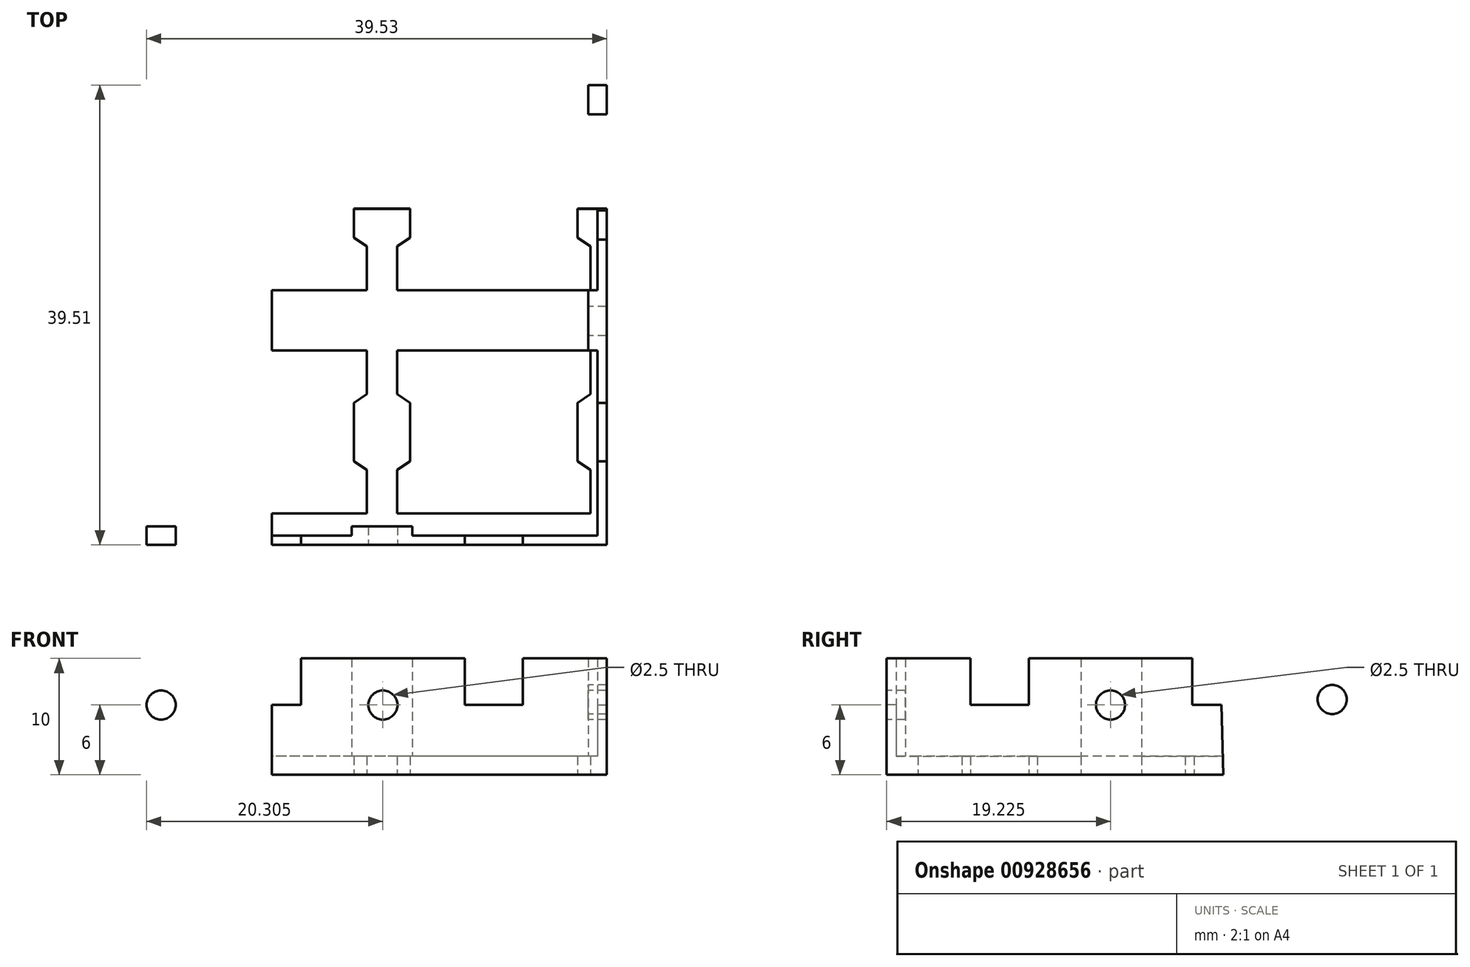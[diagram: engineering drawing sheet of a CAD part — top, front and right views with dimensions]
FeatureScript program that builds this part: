
annotation { "Feature Type Name" : "Feature", "Feature Type Description" : "" }
export const myFeature = defineFeature(function(context is Context, id is Id, definition is map)
    precondition{}
    {
        {
            var Q0;
            Q0=qCreatedBy(makeId("Top.planeOp"),FACE);
            var sketch = newSketch(context, id + "F0", { "sketchPlane" : qUnion([Q0])});
            skLineSegment(sketch, "E0.bottom", {"start": v(-1.4, 2.7) * mm, "end": v(-18, 2.7) * mm});
            skLineSegment(sketch, "E0.top", {"start": v(-1.4, 16.7) * mm, "end": v(-18, 16.7) * mm});
            skLineSegment(sketch, "E0.left", {"start": v(-1.4, 2.7) * mm, "end": v(-1.4, 16.7) * mm});
            skLineSegment(sketch, "E0.right", {"start": v(-18, 2.7) * mm, "end": v(-18, 16.7) * mm});
            skLineSegment(sketch, "E1", {"start": v(-1.4, 12.95) * mm, "end": v(-2.5, 12.2) * mm});
            skLineSegment(sketch, "E2", {"start": v(-2.5, 12.2) * mm, "end": v(-2.5, 7.2) * mm});
            skLineSegment(sketch, "E3", {"start": v(-2.5, 7.2) * mm, "end": v(-1.4, 6.45) * mm});
            skLineSegment(sketch, "E4", {"start": v(-1.4, 6.45) * mm, "end": v(-1.4, 12.95) * mm});
            skLineSegment(sketch, "E5", {"start": v(-1.4, 12.95) * mm, "end": v(-1.4, 16.7) * mm});
            skLineSegment(sketch, "E6", {"start": v(-1.4, 6.45) * mm, "end": v(-1.4, 2.7) * mm});
            skLineSegment(sketch, "E7", {"start": v(-9.7, 16.7) * mm, "end": v(-9.7, 2.7) * mm});
            skLineSegment(sketch, "E8.MirrorCS", {"start": v(-16.9, 12.2) * mm, "end": v(-16.9, 7.2) * mm});
            skLineSegment(sketch, "E9.MirrorCS", {"start": v(-18, 12.95) * mm, "end": v(-16.9, 12.2) * mm});
            skLineSegment(sketch, "E10.MirrorCS", {"start": v(-16.9, 7.2) * mm, "end": v(-18, 6.45) * mm});
            skLineSegment(sketch, "E11.1.0.0", {"start": v(-20.6, 16.7) * mm, "end": v(-37.2, 16.7) * mm});
            skLineSegment(sketch, "E11.1.0.1", {"start": v(-37.2, 2.7) * mm, "end": v(-37.2, 16.7) * mm});
            skLineSegment(sketch, "E11.1.0.2", {"start": v(-20.6, 2.7) * mm, "end": v(-37.2, 2.7) * mm});
            skLineSegment(sketch, "E11.1.0.3", {"start": v(-20.6, 6.45) * mm, "end": v(-20.6, 2.7) * mm});
            skLineSegment(sketch, "E11.1.0.4", {"start": v(-21.7, 12.2) * mm, "end": v(-21.7, 7.2) * mm});
            skLineSegment(sketch, "E11.1.0.5", {"start": v(-21.7, 7.2) * mm, "end": v(-20.6, 6.45) * mm});
            skLineSegment(sketch, "E11.1.0.6", {"start": v(-20.6, 12.95) * mm, "end": v(-21.7, 12.2) * mm});
            skLineSegment(sketch, "E11.1.0.7", {"start": v(-20.6, 12.95) * mm, "end": v(-20.6, 16.7) * mm});
            skLineSegment(sketch, "E11.1.0.8", {"start": v(-20.6, 6.45) * mm, "end": v(-20.6, 12.95) * mm});
            skLineSegment(sketch, "E11.1.0.9", {"start": v(-36.1, 12.2) * mm, "end": v(-36.1, 7.2) * mm});
            skLineSegment(sketch, "E11.1.0.10", {"start": v(-37.2, 12.95) * mm, "end": v(-36.1, 12.2) * mm});
            skLineSegment(sketch, "E11.1.0.11", {"start": v(-36.1, 7.2) * mm, "end": v(-37.2, 6.45) * mm});
            skLineSegment(sketch, "E11.2.0.0", {"start": v(-39.8, 16.7) * mm, "end": v(-56.4, 16.7) * mm});
            skLineSegment(sketch, "E11.2.0.1", {"start": v(-56.4, 2.7) * mm, "end": v(-56.4, 16.7) * mm});
            skLineSegment(sketch, "E11.2.0.2", {"start": v(-39.8, 2.7) * mm, "end": v(-56.4, 2.7) * mm});
            skLineSegment(sketch, "E11.2.0.3", {"start": v(-39.8, 6.45) * mm, "end": v(-39.8, 2.7) * mm});
            skLineSegment(sketch, "E11.2.0.4", {"start": v(-40.9, 12.2) * mm, "end": v(-40.9, 7.2) * mm});
            skLineSegment(sketch, "E11.2.0.5", {"start": v(-40.9, 7.2) * mm, "end": v(-39.8, 6.45) * mm});
            skLineSegment(sketch, "E11.2.0.6", {"start": v(-39.8, 12.95) * mm, "end": v(-40.9, 12.2) * mm});
            skLineSegment(sketch, "E11.2.0.7", {"start": v(-39.8, 12.95) * mm, "end": v(-39.8, 16.7) * mm});
            skLineSegment(sketch, "E11.2.0.8", {"start": v(-39.8, 6.45) * mm, "end": v(-39.8, 12.95) * mm});
            skLineSegment(sketch, "E11.2.0.9", {"start": v(-55.3, 12.2) * mm, "end": v(-55.3, 7.2) * mm});
            skLineSegment(sketch, "E11.2.0.10", {"start": v(-56.4, 12.95) * mm, "end": v(-55.3, 12.2) * mm});
            skLineSegment(sketch, "E11.2.0.11", {"start": v(-55.3, 7.2) * mm, "end": v(-56.4, 6.45) * mm});
            skLineSegment(sketch, "E11.direction1", {"start": v(-18, 16.7) * mm, "end": v(-37.2, 16.7) * mm, "construction": true});
            skLineSegment(sketch, "E12.bottom", {"start": v(0, 0) * mm, "end": v(-57.8, 0) * mm});
            skLineSegment(sketch, "E12.top", {"start": v(0, 57.8) * mm, "end": v(-57.8, 57.8) * mm});
            skLineSegment(sketch, "E12.left", {"start": v(0, 0) * mm, "end": v(0, 57.8) * mm});
            skLineSegment(sketch, "E12.right", {"start": v(-57.8, 0) * mm, "end": v(-57.8, 57.8) * mm});
            skLineSegment(sketch, "E13", {"start": v(-1.4, 2.7) * mm, "end": v(0, 2.7) * mm});
            skLineSegment(sketch, "E14", {"start": v(-56.4, 2.7) * mm, "end": v(-57.8, 2.7) * mm});
            skLineSegment(sketch, "E15", {"start": v(-1.4, 2.7) * mm, "end": v(-1.4, 0) * mm});
            skLineSegment(sketch, "E16.0.1.0", {"start": v(-39.8, 32.15) * mm, "end": v(-39.8, 35.9) * mm});
            skLineSegment(sketch, "E16.0.1.1", {"start": v(-20.6, 25.65) * mm, "end": v(-20.6, 21.9) * mm});
            skLineSegment(sketch, "E16.0.1.3", {"start": v(-40.9, 31.4) * mm, "end": v(-40.9, 26.4) * mm});
            skLineSegment(sketch, "E16.0.1.4", {"start": v(-1.4, 35.9) * mm, "end": v(-18, 35.9) * mm});
            skLineSegment(sketch, "E16.0.1.5", {"start": v(-1.4, 32.15) * mm, "end": v(-1.4, 35.9) * mm});
            skLineSegment(sketch, "E16.0.1.6", {"start": v(-1.4, 21.9) * mm, "end": v(-18, 21.9) * mm});
            skLineSegment(sketch, "E16.0.1.7", {"start": v(-39.8, 21.9) * mm, "end": v(-56.4, 21.9) * mm});
            skLineSegment(sketch, "E16.0.1.8", {"start": v(-36.1, 31.4) * mm, "end": v(-36.1, 26.4) * mm});
            skLineSegment(sketch, "E16.0.1.9", {"start": v(-39.8, 25.65) * mm, "end": v(-39.8, 21.9) * mm});
            skLineSegment(sketch, "E16.0.1.10", {"start": v(-21.7, 31.4) * mm, "end": v(-21.7, 26.4) * mm});
            skLineSegment(sketch, "E16.0.1.11", {"start": v(-20.6, 32.15) * mm, "end": v(-20.6, 35.9) * mm});
            skLineSegment(sketch, "E16.0.1.12", {"start": v(-20.6, 21.9) * mm, "end": v(-37.2, 21.9) * mm});
            skLineSegment(sketch, "E16.0.1.13", {"start": v(-55.3, 31.4) * mm, "end": v(-55.3, 26.4) * mm});
            skLineSegment(sketch, "E16.0.1.14", {"start": v(-20.6, 25.65) * mm, "end": v(-20.6, 32.15) * mm});
            skLineSegment(sketch, "E16.0.1.15", {"start": v(-2.5, 31.4) * mm, "end": v(-2.5, 26.4) * mm});
            skLineSegment(sketch, "E16.0.1.16", {"start": v(-16.9, 31.4) * mm, "end": v(-16.9, 26.4) * mm});
            skLineSegment(sketch, "E16.0.1.18", {"start": v(-1.4, 25.65) * mm, "end": v(-1.4, 21.9) * mm});
            skLineSegment(sketch, "E16.0.1.19", {"start": v(-39.8, 35.9) * mm, "end": v(-56.4, 35.9) * mm});
            skLineSegment(sketch, "E16.0.1.20", {"start": v(-1.4, 25.65) * mm, "end": v(-1.4, 32.15) * mm});
            skLineSegment(sketch, "E16.0.1.21", {"start": v(-18, 32.15) * mm, "end": v(-16.9, 31.4) * mm});
            skLineSegment(sketch, "E16.0.1.22", {"start": v(-37.2, 32.15) * mm, "end": v(-36.1, 31.4) * mm});
            skLineSegment(sketch, "E16.0.1.23", {"start": v(-1.4, 32.15) * mm, "end": v(-2.5, 31.4) * mm});
            skLineSegment(sketch, "E16.0.1.24", {"start": v(-20.6, 35.9) * mm, "end": v(-37.2, 35.9) * mm});
            skLineSegment(sketch, "E16.0.1.25", {"start": v(-16.9, 26.4) * mm, "end": v(-18, 25.65) * mm});
            skLineSegment(sketch, "E16.0.1.27", {"start": v(-2.5, 26.4) * mm, "end": v(-1.4, 25.65) * mm});
            skLineSegment(sketch, "E16.0.1.28", {"start": v(-36.1, 26.4) * mm, "end": v(-37.2, 25.65) * mm});
            skLineSegment(sketch, "E16.0.1.29", {"start": v(-40.9, 26.4) * mm, "end": v(-39.8, 25.65) * mm});
            skLineSegment(sketch, "E16.0.1.30", {"start": v(-20.6, 32.15) * mm, "end": v(-21.7, 31.4) * mm});
            skLineSegment(sketch, "E16.0.1.31", {"start": v(-56.4, 32.15) * mm, "end": v(-55.3, 31.4) * mm});
            skLineSegment(sketch, "E16.0.1.32", {"start": v(-21.7, 26.4) * mm, "end": v(-20.6, 25.65) * mm});
            skLineSegment(sketch, "E16.0.1.33", {"start": v(-39.8, 32.15) * mm, "end": v(-40.9, 31.4) * mm});
            skLineSegment(sketch, "E16.0.1.34", {"start": v(-55.3, 26.4) * mm, "end": v(-56.4, 25.65) * mm});
            skLineSegment(sketch, "E16.0.1.36", {"start": v(-39.8, 25.65) * mm, "end": v(-39.8, 32.15) * mm});
            skLineSegment(sketch, "E16.0.2.0", {"start": v(-39.8, 51.35) * mm, "end": v(-39.8, 55.1) * mm});
            skLineSegment(sketch, "E16.0.2.1", {"start": v(-20.6, 44.85) * mm, "end": v(-20.6, 41.1) * mm});
            skLineSegment(sketch, "E16.0.2.2", {"start": v(-18, 41.1) * mm, "end": v(-18, 55.1) * mm});
            skLineSegment(sketch, "E16.0.2.3", {"start": v(-40.9, 50.6) * mm, "end": v(-40.9, 45.6) * mm});
            skLineSegment(sketch, "E16.0.2.4", {"start": v(-1.4, 55.1) * mm, "end": v(-18, 55.1) * mm});
            skLineSegment(sketch, "E16.0.2.5", {"start": v(-1.4, 51.35) * mm, "end": v(-1.4, 55.1) * mm});
            skLineSegment(sketch, "E16.0.2.6", {"start": v(-1.4, 41.1) * mm, "end": v(-18, 41.1) * mm});
            skLineSegment(sketch, "E16.0.2.7", {"start": v(-39.8, 41.1) * mm, "end": v(-56.4, 41.1) * mm});
            skLineSegment(sketch, "E16.0.2.8", {"start": v(-36.1, 50.6) * mm, "end": v(-36.1, 45.6) * mm});
            skLineSegment(sketch, "E16.0.2.9", {"start": v(-39.8, 44.85) * mm, "end": v(-39.8, 41.1) * mm});
            skLineSegment(sketch, "E16.0.2.10", {"start": v(-21.7, 50.6) * mm, "end": v(-21.7, 45.6) * mm});
            skLineSegment(sketch, "E16.0.2.11", {"start": v(-20.6, 51.35) * mm, "end": v(-20.6, 55.1) * mm});
            skLineSegment(sketch, "E16.0.2.12", {"start": v(-20.6, 41.1) * mm, "end": v(-37.2, 41.1) * mm});
            skLineSegment(sketch, "E16.0.2.13", {"start": v(-55.3, 50.6) * mm, "end": v(-55.3, 45.6) * mm});
            skLineSegment(sketch, "E16.0.2.14", {"start": v(-20.6, 44.85) * mm, "end": v(-20.6, 51.35) * mm});
            skLineSegment(sketch, "E16.0.2.15", {"start": v(-2.5, 50.6) * mm, "end": v(-2.5, 45.6) * mm});
            skLineSegment(sketch, "E16.0.2.16", {"start": v(-16.9, 50.6) * mm, "end": v(-16.9, 45.6) * mm});
            skLineSegment(sketch, "E16.0.2.17", {"start": v(-37.2, 41.1) * mm, "end": v(-37.2, 55.1) * mm});
            skLineSegment(sketch, "E16.0.2.18", {"start": v(-1.4, 44.85) * mm, "end": v(-1.4, 41.1) * mm});
            skLineSegment(sketch, "E16.0.2.19", {"start": v(-39.8, 55.1) * mm, "end": v(-56.4, 55.1) * mm});
            skLineSegment(sketch, "E16.0.2.20", {"start": v(-1.4, 44.85) * mm, "end": v(-1.4, 51.35) * mm});
            skLineSegment(sketch, "E16.0.2.21", {"start": v(-18, 51.35) * mm, "end": v(-16.9, 50.6) * mm});
            skLineSegment(sketch, "E16.0.2.22", {"start": v(-37.2, 51.35) * mm, "end": v(-36.1, 50.6) * mm});
            skLineSegment(sketch, "E16.0.2.23", {"start": v(-1.4, 51.35) * mm, "end": v(-2.5, 50.6) * mm});
            skLineSegment(sketch, "E16.0.2.24", {"start": v(-20.6, 55.1) * mm, "end": v(-37.2, 55.1) * mm});
            skLineSegment(sketch, "E16.0.2.25", {"start": v(-16.9, 45.6) * mm, "end": v(-18, 44.85) * mm});
            skLineSegment(sketch, "E16.0.2.26", {"start": v(-1.4, 41.1) * mm, "end": v(-1.4, 55.1) * mm});
            skLineSegment(sketch, "E16.0.2.27", {"start": v(-2.5, 45.6) * mm, "end": v(-1.4, 44.85) * mm});
            skLineSegment(sketch, "E16.0.2.28", {"start": v(-36.1, 45.6) * mm, "end": v(-37.2, 44.85) * mm});
            skLineSegment(sketch, "E16.0.2.29", {"start": v(-40.9, 45.6) * mm, "end": v(-39.8, 44.85) * mm});
            skLineSegment(sketch, "E16.0.2.30", {"start": v(-20.6, 51.35) * mm, "end": v(-21.7, 50.6) * mm});
            skLineSegment(sketch, "E16.0.2.31", {"start": v(-56.4, 51.35) * mm, "end": v(-55.3, 50.6) * mm});
            skLineSegment(sketch, "E16.0.2.32", {"start": v(-21.7, 45.6) * mm, "end": v(-20.6, 44.85) * mm});
            skLineSegment(sketch, "E16.0.2.33", {"start": v(-39.8, 51.35) * mm, "end": v(-40.9, 50.6) * mm});
            skLineSegment(sketch, "E16.0.2.34", {"start": v(-55.3, 45.6) * mm, "end": v(-56.4, 44.85) * mm});
            skLineSegment(sketch, "E16.0.2.35", {"start": v(-56.4, 41.1) * mm, "end": v(-56.4, 55.1) * mm});
            skLineSegment(sketch, "E16.0.2.36", {"start": v(-39.8, 44.85) * mm, "end": v(-39.8, 51.35) * mm});
            skLineSegment(sketch, "E16.direction1", {"start": v(-56.4, 2.7) * mm, "end": v(-34.05, 2.7) * mm, "construction": true});
            skLineSegment(sketch, "E16.direction2", {"start": v(-56.4, 2.7) * mm, "end": v(-56.4, 21.9) * mm, "construction": true});
            skLineSegment(sketch, "E17", {"start": v(-1.4, 55.1) * mm, "end": v(-1.4, 57.8) * mm});
            skLineSegment(sketch, "E18", {"start": v(-56.4, 12.95) * mm, "end": v(-56.4, 16.7) * mm});
            skLineSegment(sketch, "E19", {"start": v(-56.4, 32.15) * mm, "end": v(-56.4, 35.9) * mm});
            skLineSegment(sketch, "E20", {"start": v(-56.4, 25.65) * mm, "end": v(-56.4, 21.9) * mm});
            skLineSegment(sketch, "E21", {"start": v(-37.2, 25.65) * mm, "end": v(-37.2, 21.9) * mm});
            skLineSegment(sketch, "E22", {"start": v(-37.2, 32.15) * mm, "end": v(-37.2, 35.9) * mm});
            skLineSegment(sketch, "E23", {"start": v(-18, 35.9) * mm, "end": v(-18, 32.15) * mm});
            skLineSegment(sketch, "E24", {"start": v(-18, 25.65) * mm, "end": v(-18, 21.9) * mm});
            skLineSegment(sketch, "E25", {"start": v(-56.4, 32.15) * mm, "end": v(-56.4, 25.65) * mm});
            skLineSegment(sketch, "E26", {"start": v(-37.2, 25.65) * mm, "end": v(-37.2, 32.15) * mm});
            skLineSegment(sketch, "E27", {"start": v(-18, 25.65) * mm, "end": v(-18, 32.15) * mm});
            skLineSegment(sketch, "E28.0", {"start": v(-39.55, 32.02) * mm, "end": v(-39.55, 36.15) * mm});
            skLineSegment(sketch, "E28.1", {"start": v(-55.55, 26.53) * mm, "end": v(-56.65, 25.78) * mm});
            skLineSegment(sketch, "E28.2", {"start": v(-55.55, 31.27) * mm, "end": v(-55.55, 26.53) * mm});
            skLineSegment(sketch, "E28.3", {"start": v(-56.65, 32.02) * mm, "end": v(-55.55, 31.27) * mm});
            skLineSegment(sketch, "E28.4", {"start": v(-56.65, 32.02) * mm, "end": v(-56.65, 36.15) * mm});
            skLineSegment(sketch, "E28.5", {"start": v(-56.65, 25.78) * mm, "end": v(-56.65, 21.65) * mm});
            skLineSegment(sketch, "E28.6", {"start": v(-39.55, 36.15) * mm, "end": v(-56.65, 36.15) * mm});
            skLineSegment(sketch, "E28.7", {"start": v(-39.55, 21.65) * mm, "end": v(-56.65, 21.65) * mm});
            skLineSegment(sketch, "E28.8", {"start": v(-39.55, 25.78) * mm, "end": v(-39.55, 21.65) * mm});
            skLineSegment(sketch, "E28.9", {"start": v(-40.65, 26.53) * mm, "end": v(-39.55, 25.78) * mm});
            skLineSegment(sketch, "E28.10", {"start": v(-40.65, 31.27) * mm, "end": v(-40.65, 26.53) * mm});
            skLineSegment(sketch, "E28.11", {"start": v(-39.55, 32.02) * mm, "end": v(-40.65, 31.27) * mm});
            skLineSegment(sketch, "E29.0", {"start": v(-20.35, 32.02) * mm, "end": v(-20.35, 36.15) * mm});
            skLineSegment(sketch, "E29.1", {"start": v(-36.35, 26.53) * mm, "end": v(-37.45, 25.78) * mm});
            skLineSegment(sketch, "E29.2", {"start": v(-36.35, 31.27) * mm, "end": v(-36.35, 26.53) * mm});
            skLineSegment(sketch, "E29.3", {"start": v(-37.45, 32.02) * mm, "end": v(-36.35, 31.27) * mm});
            skLineSegment(sketch, "E29.4", {"start": v(-37.45, 32.02) * mm, "end": v(-37.45, 36.15) * mm});
            skLineSegment(sketch, "E29.5", {"start": v(-37.45, 25.78) * mm, "end": v(-37.45, 21.65) * mm});
            skLineSegment(sketch, "E29.6", {"start": v(-20.35, 36.15) * mm, "end": v(-37.45, 36.15) * mm});
            skLineSegment(sketch, "E29.7", {"start": v(-20.35, 21.65) * mm, "end": v(-37.45, 21.65) * mm});
            skLineSegment(sketch, "E29.8", {"start": v(-20.35, 25.78) * mm, "end": v(-20.35, 21.65) * mm});
            skLineSegment(sketch, "E29.9", {"start": v(-21.45, 26.53) * mm, "end": v(-20.35, 25.78) * mm});
            skLineSegment(sketch, "E29.10", {"start": v(-21.45, 31.27) * mm, "end": v(-21.45, 26.53) * mm});
            skLineSegment(sketch, "E29.11", {"start": v(-20.35, 32.02) * mm, "end": v(-21.45, 31.27) * mm});
            skLineSegment(sketch, "E30.0", {"start": v(-1.15, 32.02) * mm, "end": v(-1.15, 36.15) * mm});
            skLineSegment(sketch, "E30.1", {"start": v(-17.15, 26.53) * mm, "end": v(-18.25, 25.78) * mm});
            skLineSegment(sketch, "E30.2", {"start": v(-17.15, 31.27) * mm, "end": v(-17.15, 26.53) * mm});
            skLineSegment(sketch, "E30.3", {"start": v(-18.25, 32.02) * mm, "end": v(-17.15, 31.27) * mm});
            skLineSegment(sketch, "E30.4", {"start": v(-18.25, 36.15) * mm, "end": v(-18.25, 32.02) * mm});
            skLineSegment(sketch, "E30.5", {"start": v(-18.25, 25.78) * mm, "end": v(-18.25, 21.65) * mm});
            skLineSegment(sketch, "E30.6", {"start": v(-1.15, 36.15) * mm, "end": v(-18.25, 36.15) * mm});
            skLineSegment(sketch, "E30.7", {"start": v(-1.15, 21.65) * mm, "end": v(-18.25, 21.65) * mm});
            skLineSegment(sketch, "E30.8", {"start": v(-1.15, 25.78) * mm, "end": v(-1.15, 21.65) * mm});
            skLineSegment(sketch, "E30.9", {"start": v(-2.25, 26.53) * mm, "end": v(-1.15, 25.78) * mm});
            skLineSegment(sketch, "E30.10", {"start": v(-2.25, 31.27) * mm, "end": v(-2.25, 26.53) * mm});
            skLineSegment(sketch, "E30.11", {"start": v(-1.15, 32.02) * mm, "end": v(-2.25, 31.27) * mm});
            skSolve(sketch);
        }
        {
            var Q0;
            {var subQ4=sQuery(id+"F0.wireOp",EDGE,"E13");Q0=makeQuery(id+"F0.imprint","IMPRINT",FACE,{"disambiguationData":[TD([[makeQuery(id+"F0.imprint","IMPRINT",EDGE,{"derivedFrom":subQ4}),-1.0]])]});}
            var Q1;
            Q1=makeQuery(id+"F0.imprint","IMPRINT",FACE,{"disambiguationData":[TD([[makeQuery(id+"F0.imprint","IMPRINT",EDGE,{"derivedFrom":sQuery(id+"F0.wireOp",EDGE,"E11.1.0.9")}),-1.0]])]});
            var Q2;
            Q2=makeQuery(id+"F0.imprint","IMPRINT",FACE,{"disambiguationData":[TD([[makeQuery(id+"F0.imprint","IMPRINT",EDGE,{"derivedFrom":sQuery(id+"F0.wireOp",EDGE,"E11.2.0.4")}),1.0]])]});
            var Q3;
            Q3=makeQuery(id+"F0.imprint","IMPRINT",FACE,{"disambiguationData":[TD([[makeQuery(id+"F0.imprint","IMPRINT",EDGE,{"derivedFrom":sQuery(id+"F0.wireOp",EDGE,"437544f1-30d8-4290-8c43-db503dbb5188.0.1.24")}),-1.0]])]});
            var Q4;
            Q4=makeQuery(id+"F0.imprint","IMPRINT",FACE,{"disambiguationData":[TD([[makeQuery(id+"F0.imprint","IMPRINT",EDGE,{"derivedFrom":sQuery(id+"F0.wireOp",EDGE,"437544f1-30d8-4290-8c43-db503dbb5188.0.1.14")}),1.0]])]});
            var Q5;
            Q5=makeQuery(id+"F0.imprint","IMPRINT",FACE,{"disambiguationData":[TD([[makeQuery(id+"F0.imprint","IMPRINT",EDGE,{"derivedFrom":sQuery(id+"F0.wireOp",EDGE,"437544f1-30d8-4290-8c43-db503dbb5188.0.1.10")}),-1.0]])]});
            var Q6;
            Q6=makeQuery(id+"F0.imprint","IMPRINT",FACE,{"disambiguationData":[TD([[makeQuery(id+"F0.imprint","IMPRINT",EDGE,{"derivedFrom":sQuery(id+"F0.wireOp",EDGE,"437544f1-30d8-4290-8c43-db503dbb5188.0.1.7")}),1.0]])]});
            var Q7;
            Q7=makeQuery(id+"F0.imprint","IMPRINT",FACE,{"disambiguationData":[TD([[makeQuery(id+"F0.imprint","IMPRINT",EDGE,{"derivedFrom":sQuery(id+"F0.wireOp",EDGE,"437544f1-30d8-4290-8c43-db503dbb5188.0.1.3")}),-1.0]])]});
            var Q8;
            Q8=makeQuery(id+"F0.imprint","IMPRINT",FACE,{"disambiguationData":[TD([[makeQuery(id+"F0.imprint","IMPRINT",EDGE,{"derivedFrom":sQuery(id+"F0.wireOp",EDGE,"437544f1-30d8-4290-8c43-db503dbb5188.0.1.4")}),1.0]])]});
            var Q9;
            Q9=makeQuery(id+"F0.imprint","IMPRINT",FACE,{"disambiguationData":[TD([[makeQuery(id+"F0.imprint","IMPRINT",EDGE,{"derivedFrom":sQuery(id+"F0.wireOp",EDGE,"437544f1-30d8-4290-8c43-db503dbb5188.0.2.4")}),1.0]])]});
            var Q10;
            Q10=makeQuery(id+"F0.imprint","IMPRINT",FACE,{"disambiguationData":[TD([[makeQuery(id+"F0.imprint","IMPRINT",EDGE,{"derivedFrom":sQuery(id+"F0.wireOp",EDGE,"437544f1-30d8-4290-8c43-db503dbb5188.0.2.3")}),-1.0]])]});
            var Q11;
            Q11=makeQuery(id+"F0.imprint","IMPRINT",FACE,{"disambiguationData":[TD([[makeQuery(id+"F0.imprint","IMPRINT",EDGE,{"derivedFrom":sQuery(id+"F0.wireOp",EDGE,"437544f1-30d8-4290-8c43-db503dbb5188.0.2.7")}),1.0]])]});
            var Q12;
            Q12=makeQuery(id+"F0.imprint","IMPRINT",FACE,{"disambiguationData":[TD([[makeQuery(id+"F0.imprint","IMPRINT",EDGE,{"derivedFrom":sQuery(id+"F0.wireOp",EDGE,"437544f1-30d8-4290-8c43-db503dbb5188.0.2.10")}),-1.0]])]});
            var Q13;
            Q13=makeQuery(id+"F0.imprint","IMPRINT",FACE,{"disambiguationData":[TD([[makeQuery(id+"F0.imprint","IMPRINT",EDGE,{"derivedFrom":sQuery(id+"F0.wireOp",EDGE,"437544f1-30d8-4290-8c43-db503dbb5188.0.2.14")}),1.0]])]});
            var Q14;
            Q14=makeQuery(id+"F0.imprint","IMPRINT",FACE,{"disambiguationData":[TD([[makeQuery(id+"F0.imprint","IMPRINT",EDGE,{"derivedFrom":sQuery(id+"F0.wireOp",EDGE,"437544f1-30d8-4290-8c43-db503dbb5188.0.2.24")}),-1.0]])]});
            var Q15;
            {var subQ71=sQuery(id+"F0.wireOp",EDGE,"E11.1.0.0");Q15=makeQuery(id+"F0.imprint","IMPRINT",FACE,{"disambiguationData":[TD([[makeQuery(id+"F0.imprint","IMPRINT",EDGE,{"derivedFrom":subQ71}),-1.0]])]});}
            var Q16;
            Q16=makeQuery(id+"F0.imprint","IMPRINT",FACE,{"disambiguationData":[TD([[makeQuery(id+"F0.imprint","IMPRINT",EDGE,{"derivedFrom":sQuery(id+"F0.wireOp",EDGE,"E8.MirrorCS")}),-1.0]])]});
            var Q17;
            Q17=makeQuery(id+"F0.imprint","IMPRINT",FACE,{"disambiguationData":[TD([[makeQuery(id+"F0.imprint","IMPRINT",EDGE,{"derivedFrom":sQuery(id+"F0.wireOp",EDGE,"E11.1.0.4")}),1.0]])]});
            var Q18;
            Q18=makeQuery(id+"F0.imprint","IMPRINT",FACE,{"disambiguationData":[TD([[makeQuery(id+"F0.imprint","IMPRINT",EDGE,{"derivedFrom":sQuery(id+"F0.wireOp",EDGE,"E16.0.2.8")}),-1.0]])]});
            var Q19;
            Q19=makeQuery(id+"F0.imprint","IMPRINT",FACE,{"disambiguationData":[TD([[makeQuery(id+"F0.imprint","IMPRINT",EDGE,{"derivedFrom":sQuery(id+"F0.wireOp",EDGE,"E16.0.2.15")}),1.0]])]});
            var Q20;
            {var subQ2=sQuery(id+"F0.wireOp",EDGE,"E1");Q20=makeQuery(id+"F0.imprint","IMPRINT",FACE,{"disambiguationData":[TD([[makeQuery(id+"F0.imprint","IMPRINT",EDGE,{"derivedFrom":subQ2}),1.0]])]});}
            var Q21;
            Q21=makeQuery(id+"F0.imprint","IMPRINT",FACE,{"disambiguationData":[TD([[makeQuery(id+"F0.imprint","IMPRINT",EDGE,{"derivedFrom":sQuery(id+"F0.wireOp",EDGE,"E11.2.0.9")}),-1.0]])]});
            var Q22;
            Q22=makeQuery(id+"F0.imprint","IMPRINT",FACE,{"disambiguationData":[TD([[makeQuery(id+"F0.imprint","IMPRINT",EDGE,{"derivedFrom":sQuery(id+"F0.wireOp",EDGE,"E16.0.2.16")}),-1.0]])]});
            var Q23;
            Q23=makeQuery(id+"F0.imprint","IMPRINT",FACE,{"disambiguationData":[TD([[makeQuery(id+"F0.imprint","IMPRINT",EDGE,{"derivedFrom":sQuery(id+"F0.wireOp",EDGE,"E16.0.2.10")}),1.0]])]});
            var Q24;
            Q24=makeQuery(id+"F0.imprint","IMPRINT",FACE,{"disambiguationData":[TD([[makeQuery(id+"F0.imprint","IMPRINT",EDGE,{"derivedFrom":sQuery(id+"F0.wireOp",EDGE,"E16.0.2.3")}),1.0]])]});
            var Q25;
            Q25=makeQuery(id+"F0.imprint","IMPRINT",FACE,{"disambiguationData":[TD([[makeQuery(id+"F0.imprint","IMPRINT",EDGE,{"derivedFrom":sQuery(id+"F0.wireOp",EDGE,"E16.0.2.13")}),-1.0]])]});
            var Q26;
            {var subQ5=sQuery(id+"F0.wireOp",EDGE,"E28.2");Q26=makeQuery(id+"F0.imprint","IMPRINT",FACE,{"disambiguationData":[TD([[makeQuery(id+"F0.imprint","IMPRINT",EDGE,{"derivedFrom":subQ5}),-1.0]])]});}
            var Q27;
            {var subQ5=sQuery(id+"F0.wireOp",EDGE,"E28.10");Q27=makeQuery(id+"F0.imprint","IMPRINT",FACE,{"disambiguationData":[TD([[makeQuery(id+"F0.imprint","IMPRINT",EDGE,{"derivedFrom":subQ5}),1.0]])]});}
            var Q28;
            {var subQ5=sQuery(id+"F0.wireOp",EDGE,"E29.2");Q28=makeQuery(id+"F0.imprint","IMPRINT",FACE,{"disambiguationData":[TD([[makeQuery(id+"F0.imprint","IMPRINT",EDGE,{"derivedFrom":subQ5}),-1.0]])]});}
            var Q29;
            {var subQ5=sQuery(id+"F0.wireOp",EDGE,"E29.10");Q29=makeQuery(id+"F0.imprint","IMPRINT",FACE,{"disambiguationData":[TD([[makeQuery(id+"F0.imprint","IMPRINT",EDGE,{"derivedFrom":subQ5}),1.0]])]});}
            var Q30;
            {var subQ5=sQuery(id+"F0.wireOp",EDGE,"E30.2");Q30=makeQuery(id+"F0.imprint","IMPRINT",FACE,{"disambiguationData":[TD([[makeQuery(id+"F0.imprint","IMPRINT",EDGE,{"derivedFrom":subQ5}),-1.0]])]});}
            var Q31;
            {var subQ5=sQuery(id+"F0.wireOp",EDGE,"E30.10");Q31=makeQuery(id+"F0.imprint","IMPRINT",FACE,{"disambiguationData":[TD([[makeQuery(id+"F0.imprint","IMPRINT",EDGE,{"derivedFrom":subQ5}),1.0]])]});}
            var Q32;
            Q32=makeQuery(id+"F0.imprint","IMPRINT",FACE,{"disambiguationData":[TD([[makeQuery(id+"F0.imprint","IMPRINT",EDGE,{"derivedFrom":sQuery(id+"F0.wireOp",EDGE,"E16.0.1.13")}),-1.0]])]});
            var Q33;
            {var subQ2=sQuery(id+"F0.wireOp",EDGE,"E16.0.1.0");Q33=makeQuery(id+"F0.imprint","IMPRINT",FACE,{"disambiguationData":[TD([[makeQuery(id+"F0.imprint","IMPRINT",EDGE,{"derivedFrom":subQ2}),-1.0]])]});}
            var Q34;
            Q34=makeQuery(id+"F0.imprint","IMPRINT",FACE,{"disambiguationData":[TD([[makeQuery(id+"F0.imprint","IMPRINT",EDGE,{"derivedFrom":sQuery(id+"F0.wireOp",EDGE,"E16.0.1.7")}),1.0]])]});
            var Q35;
            Q35=makeQuery(id+"F0.imprint","IMPRINT",FACE,{"disambiguationData":[TD([[makeQuery(id+"F0.imprint","IMPRINT",EDGE,{"derivedFrom":sQuery(id+"F0.wireOp",EDGE,"E16.0.1.3")}),1.0]])]});
            var Q36;
            {var subQ6=sQuery(id+"F0.wireOp",EDGE,"E16.0.1.11");Q36=makeQuery(id+"F0.imprint","IMPRINT",FACE,{"disambiguationData":[TD([[makeQuery(id+"F0.imprint","IMPRINT",EDGE,{"derivedFrom":subQ6}),-1.0]])]});}
            var Q37;
            Q37=makeQuery(id+"F0.imprint","IMPRINT",FACE,{"disambiguationData":[TD([[makeQuery(id+"F0.imprint","IMPRINT",EDGE,{"derivedFrom":sQuery(id+"F0.wireOp",EDGE,"E16.0.1.8")}),-1.0]])]});
            var Q38;
            {var subQ2=sQuery(id+"F0.wireOp",EDGE,"E16.0.1.1");Q38=makeQuery(id+"F0.imprint","IMPRINT",FACE,{"disambiguationData":[TD([[makeQuery(id+"F0.imprint","IMPRINT",EDGE,{"derivedFrom":subQ2}),1.0]])]});}
            var Q39;
            Q39=makeQuery(id+"F0.imprint","IMPRINT",FACE,{"disambiguationData":[TD([[makeQuery(id+"F0.imprint","IMPRINT",EDGE,{"derivedFrom":sQuery(id+"F0.wireOp",EDGE,"E16.0.1.10")}),1.0]])]});
            var Q40;
            Q40=makeQuery(id+"F0.imprint","IMPRINT",FACE,{"disambiguationData":[TD([[makeQuery(id+"F0.imprint","IMPRINT",EDGE,{"derivedFrom":sQuery(id+"F0.wireOp",EDGE,"E16.0.1.16")}),-1.0]])]});
            var Q41;
            Q41=makeQuery(id+"F0.imprint","IMPRINT",FACE,{"disambiguationData":[TD([[makeQuery(id+"F0.imprint","IMPRINT",EDGE,{"derivedFrom":sQuery(id+"F0.wireOp",EDGE,"E16.0.1.4")}),-1.0]])]});
            var Q42;
            Q42=makeQuery(id+"F0.imprint","IMPRINT",FACE,{"disambiguationData":[TD([[makeQuery(id+"F0.imprint","IMPRINT",EDGE,{"derivedFrom":sQuery(id+"F0.wireOp",EDGE,"E16.0.1.15")}),1.0]])]});
            var Q43;
            Q43=makeQuery(id+"F0.imprint","IMPRINT",FACE,{"disambiguationData":[TD([[makeQuery(id+"F0.imprint","IMPRINT",EDGE,{"derivedFrom":sQuery(id+"F0.wireOp",EDGE,"E16.0.1.6")}),1.0]])]});
            extrude(context, id + "F1", {"entities" : qUnion([Q0, Q1, Q2, Q3, Q4, Q5, Q6, Q7, Q8, Q9, Q10, Q11, Q12, Q13, Q14, Q15, Q16, Q17, Q18, Q19, Q20, Q21, Q22, Q23, Q24, Q25, Q26, Q27, Q28, Q29, Q30, Q31, Q32, Q33, Q34, Q35, Q36, Q37, Q38, Q39, Q40, Q41, Q42, Q43]), "depth" : 1.6 * mm, "offsetDistance" : 25 * mm});
        }
        {
            var Q0;
            Q0=makeQuery(id+"F1.opExtrude","CAP_FACE",FACE,{"disambiguationData":[OSD([sQuery(id+"F0.wireOp",EDGE,"E0.bottom"),sQuery(id+"F0.wireOp",EDGE,"E0.top"),sQuery(id+"F0.wireOp",EDGE,"E0.left"),sQuery(id+"F0.wireOp",EDGE,"E0.right"),sQuery(id+"F0.wireOp",EDGE,"E1"),sQuery(id+"F0.wireOp",EDGE,"E2"),sQuery(id+"F0.wireOp",EDGE,"E3"),sQuery(id+"F0.wireOp",EDGE,"E8.MirrorCS"),sQuery(id+"F0.wireOp",EDGE,"E9.MirrorCS"),sQuery(id+"F0.wireOp",EDGE,"E10.MirrorCS"),sQuery(id+"F0.wireOp",EDGE,"E11.1.0.0"),sQuery(id+"F0.wireOp",EDGE,"E11.1.0.1"),sQuery(id+"F0.wireOp",EDGE,"E11.1.0.2"),sQuery(id+"F0.wireOp",EDGE,"E11.1.0.3"),sQuery(id+"F0.wireOp",EDGE,"E11.1.0.4"),sQuery(id+"F0.wireOp",EDGE,"E11.1.0.5"),sQuery(id+"F0.wireOp",EDGE,"E11.1.0.6"),sQuery(id+"F0.wireOp",EDGE,"E11.1.0.7"),sQuery(id+"F0.wireOp",EDGE,"E11.1.0.9"),sQuery(id+"F0.wireOp",EDGE,"E11.1.0.10"),sQuery(id+"F0.wireOp",EDGE,"E11.1.0.11"),sQuery(id+"F0.wireOp",EDGE,"E11.2.0.0"),sQuery(id+"F0.wireOp",EDGE,"E11.2.0.1"),sQuery(id+"F0.wireOp",EDGE,"E11.2.0.2"),sQuery(id+"F0.wireOp",EDGE,"E11.2.0.3"),sQuery(id+"F0.wireOp",EDGE,"E11.2.0.4"),sQuery(id+"F0.wireOp",EDGE,"E11.2.0.5"),sQuery(id+"F0.wireOp",EDGE,"E11.2.0.6"),sQuery(id+"F0.wireOp",EDGE,"E11.2.0.7"),sQuery(id+"F0.wireOp",EDGE,"E11.2.0.9"),sQuery(id+"F0.wireOp",EDGE,"E11.2.0.10"),sQuery(id+"F0.wireOp",EDGE,"E11.2.0.11"),sQuery(id+"F0.wireOp",EDGE,"E12.bottom"),sQuery(id+"F0.wireOp",EDGE,"E12.top"),sQuery(id+"F0.wireOp",EDGE,"E12.left"),sQuery(id+"F0.wireOp",EDGE,"E12.right"),sQuery(id+"F0.wireOp",EDGE,"E16.0.2.0"),sQuery(id+"F0.wireOp",EDGE,"E16.0.2.1"),sQuery(id+"F0.wireOp",EDGE,"E16.0.2.2"),sQuery(id+"F0.wireOp",EDGE,"E16.0.2.3"),sQuery(id+"F0.wireOp",EDGE,"E16.0.2.4"),sQuery(id+"F0.wireOp",EDGE,"E16.0.2.5"),sQuery(id+"F0.wireOp",EDGE,"E16.0.2.6"),sQuery(id+"F0.wireOp",EDGE,"E16.0.2.7"),sQuery(id+"F0.wireOp",EDGE,"E16.0.2.8"),sQuery(id+"F0.wireOp",EDGE,"E16.0.2.9"),sQuery(id+"F0.wireOp",EDGE,"E16.0.2.10"),sQuery(id+"F0.wireOp",EDGE,"E16.0.2.11"),sQuery(id+"F0.wireOp",EDGE,"E16.0.2.12"),sQuery(id+"F0.wireOp",EDGE,"E16.0.2.13"),sQuery(id+"F0.wireOp",EDGE,"E16.0.2.15"),sQuery(id+"F0.wireOp",EDGE,"E16.0.2.16"),sQuery(id+"F0.wireOp",EDGE,"E16.0.2.17"),sQuery(id+"F0.wireOp",EDGE,"E16.0.2.18"),sQuery(id+"F0.wireOp",EDGE,"E16.0.2.19"),sQuery(id+"F0.wireOp",EDGE,"E16.0.2.21"),sQuery(id+"F0.wireOp",EDGE,"E16.0.2.22"),sQuery(id+"F0.wireOp",EDGE,"E16.0.2.23"),sQuery(id+"F0.wireOp",EDGE,"E16.0.2.24"),sQuery(id+"F0.wireOp",EDGE,"E16.0.2.25"),sQuery(id+"F0.wireOp",EDGE,"E16.0.2.27"),sQuery(id+"F0.wireOp",EDGE,"E16.0.2.28"),sQuery(id+"F0.wireOp",EDGE,"E16.0.2.29"),sQuery(id+"F0.wireOp",EDGE,"E16.0.2.30"),sQuery(id+"F0.wireOp",EDGE,"E16.0.2.31"),sQuery(id+"F0.wireOp",EDGE,"E16.0.2.32"),sQuery(id+"F0.wireOp",EDGE,"E16.0.2.33"),sQuery(id+"F0.wireOp",EDGE,"E16.0.2.34"),sQuery(id+"F0.wireOp",EDGE,"E16.0.2.35"),sQuery(id+"F0.wireOp",EDGE,"E28.0"),sQuery(id+"F0.wireOp",EDGE,"E28.1"),sQuery(id+"F0.wireOp",EDGE,"E28.2"),sQuery(id+"F0.wireOp",EDGE,"E28.3"),sQuery(id+"F0.wireOp",EDGE,"E28.4"),sQuery(id+"F0.wireOp",EDGE,"E28.5"),sQuery(id+"F0.wireOp",EDGE,"E28.6"),sQuery(id+"F0.wireOp",EDGE,"E28.7"),sQuery(id+"F0.wireOp",EDGE,"E28.8"),sQuery(id+"F0.wireOp",EDGE,"E28.9"),sQuery(id+"F0.wireOp",EDGE,"E28.10"),sQuery(id+"F0.wireOp",EDGE,"E28.11"),sQuery(id+"F0.wireOp",EDGE,"E29.0"),sQuery(id+"F0.wireOp",EDGE,"E29.1"),sQuery(id+"F0.wireOp",EDGE,"E29.2"),sQuery(id+"F0.wireOp",EDGE,"E29.3"),sQuery(id+"F0.wireOp",EDGE,"E29.4"),sQuery(id+"F0.wireOp",EDGE,"E29.5"),sQuery(id+"F0.wireOp",EDGE,"E29.6"),sQuery(id+"F0.wireOp",EDGE,"E29.7"),sQuery(id+"F0.wireOp",EDGE,"E29.8"),sQuery(id+"F0.wireOp",EDGE,"E29.9"),sQuery(id+"F0.wireOp",EDGE,"E29.10"),sQuery(id+"F0.wireOp",EDGE,"E29.11"),sQuery(id+"F0.wireOp",EDGE,"E30.0"),sQuery(id+"F0.wireOp",EDGE,"E30.1"),sQuery(id+"F0.wireOp",EDGE,"E30.2"),sQuery(id+"F0.wireOp",EDGE,"E30.3"),sQuery(id+"F0.wireOp",EDGE,"E30.4"),sQuery(id+"F0.wireOp",EDGE,"E30.5"),sQuery(id+"F0.wireOp",EDGE,"E30.6"),sQuery(id+"F0.wireOp",EDGE,"E30.7"),sQuery(id+"F0.wireOp",EDGE,"E30.8"),sQuery(id+"F0.wireOp",EDGE,"E30.9"),sQuery(id+"F0.wireOp",EDGE,"E30.10"),sQuery(id+"F0.wireOp",EDGE,"E30.11")])],"isStart":false});
            var sketch = newSketch(context, id + "F2", { "sketchPlane" : qUnion([Q0])});
            skLineSegment(sketch, "E31.bottom", {"start": v(0, 0) * mm, "end": v(-57.8, 0) * mm});
            skLineSegment(sketch, "E31.top", {"start": v(0, 57.8) * mm, "end": v(-57.8, 57.8) * mm});
            skLineSegment(sketch, "E31.left", {"start": v(0, 0) * mm, "end": v(0, 57.8) * mm});
            skLineSegment(sketch, "E31.right", {"start": v(-57.8, 0) * mm, "end": v(-57.8, 57.8) * mm});
            skLineSegment(sketch, "E32.0", {"start": v(-0.8, 57) * mm, "end": v(-57, 57) * mm});
            skLineSegment(sketch, "E32.1", {"start": v(-0.8, 0.8) * mm, "end": v(-0.8, 57) * mm});
            skLineSegment(sketch, "E32.2", {"start": v(-0.8, 0.8) * mm, "end": v(-57, 0.8) * mm});
            skLineSegment(sketch, "E32.3", {"start": v(-57, 0.8) * mm, "end": v(-57, 57) * mm});
            skLineSegment(sketch, "E33", {"start": v(-2.5, 9.7) * mm, "end": v(-0.8, 9.7) * mm});
            skLineSegment(sketch, "E34", {"start": v(-0.8, 9.7) * mm, "end": v(0, 9.7) * mm});
            skLineSegment(sketch, "E35", {"start": v(-0.8, 9.7) * mm, "end": v(-0.8, 7.2) * mm});
            skLineSegment(sketch, "E36", {"start": v(-0.8, 7.2) * mm, "end": v(0, 7.2) * mm});
            skLineSegment(sketch, "E37", {"start": v(0, 7.2) * mm, "end": v(0, 9.7) * mm});
            skLineSegment(sketch, "E38.MirrorCS", {"start": v(-0.8, 12.2) * mm, "end": v(0, 12.2) * mm});
            skLineSegment(sketch, "E39.direction2", {"start": v(-0.8, 12.2) * mm, "end": v(-0.8, 31.07) * mm, "construction": true});
            skLineSegment(sketch, "E40", {"start": v(-28.9, 0) * mm, "end": v(-28.9, 0.8) * mm});
            skLineSegment(sketch, "E41.0.1.0", {"start": v(-0.8, 31.25) * mm, "end": v(0, 31.25) * mm});
            skLineSegment(sketch, "E41.0.1.1", {"start": v(-0.8, 26.25) * mm, "end": v(0, 26.25) * mm});
            skLineSegment(sketch, "E41.0.2.0", {"start": v(-0.8, 50.3) * mm, "end": v(0, 50.3) * mm});
            skLineSegment(sketch, "E41.0.2.1", {"start": v(-0.8, 45.3) * mm, "end": v(0, 45.3) * mm});
            skLineSegment(sketch, "E41.direction1", {"start": v(-0.8, 12.2) * mm, "end": v(-9.9, 12.2) * mm, "construction": true});
            skLineSegment(sketch, "E41.direction2", {"start": v(-0.8, 12.2) * mm, "end": v(-0.8, 31.25) * mm, "construction": true});
            skLineSegment(sketch, "E42.MirrorCS", {"start": v(-57, 7.2) * mm, "end": v(-57.8, 7.2) * mm});
            skLineSegment(sketch, "E43.MirrorCS", {"start": v(-57, 12.2) * mm, "end": v(-57.8, 12.2) * mm});
            skLineSegment(sketch, "E44.MirrorCS", {"start": v(-57, 26.25) * mm, "end": v(-57.8, 26.25) * mm});
            skLineSegment(sketch, "E45.MirrorCS", {"start": v(-57, 31.25) * mm, "end": v(-57.8, 31.25) * mm});
            skLineSegment(sketch, "E46.MirrorCS", {"start": v(-57, 45.3) * mm, "end": v(-57.8, 45.3) * mm});
            skLineSegment(sketch, "E47.MirrorCS", {"start": v(-57, 50.3) * mm, "end": v(-57.8, 50.3) * mm});
            skLineSegment(sketch, "E48", {"start": v(-9.7, 2.7) * mm, "end": v(-9.7, 0.8) * mm});
            skLineSegment(sketch, "E49", {"start": v(-9.7, 0.8) * mm, "end": v(-9.7, 0) * mm});
            skLineSegment(sketch, "E50", {"start": v(-9.7, 0) * mm, "end": v(-7.2, 0) * mm});
            skLineSegment(sketch, "E51", {"start": v(-7.2, 0) * mm, "end": v(-7.2, 0.8) * mm});
            skLineSegment(sketch, "E52", {"start": v(-7.2, 0.8) * mm, "end": v(-9.7, 0.8) * mm});
            skLineSegment(sketch, "E53", {"start": v(-9.7, 0.8) * mm, "end": v(-12.2, 0.8) * mm});
            skLineSegment(sketch, "E54", {"start": v(-12.2, 0.8) * mm, "end": v(-12.2, 0) * mm});
            skLineSegment(sketch, "E55", {"start": v(-12.2, 0) * mm, "end": v(-9.7, 0) * mm});
            skLineSegment(sketch, "E56", {"start": v(0, 28.9) * mm, "end": v(-0.8, 28.9) * mm});
            skLineSegment(sketch, "E57.1.0.0", {"start": v(-31.25, 0.8) * mm, "end": v(-31.25, 0) * mm});
            skLineSegment(sketch, "E57.1.0.1", {"start": v(-26.25, 0) * mm, "end": v(-26.25, 0.8) * mm});
            skLineSegment(sketch, "E57.2.0.0", {"start": v(-50.3, 0.8) * mm, "end": v(-50.3, 0) * mm});
            skLineSegment(sketch, "E57.2.0.1", {"start": v(-45.3, 0) * mm, "end": v(-45.3, 0.8) * mm});
            skLineSegment(sketch, "E57.direction1", {"start": v(-12.2, 0) * mm, "end": v(-31.25, 0) * mm, "construction": true});
            skLineSegment(sketch, "E58.MirrorCS", {"start": v(-12.2, 57) * mm, "end": v(-12.2, 57.8) * mm});
            skLineSegment(sketch, "E59.MirrorCS", {"start": v(-7.2, 57.8) * mm, "end": v(-7.2, 57) * mm});
            skLineSegment(sketch, "E60.MirrorCS", {"start": v(-26.25, 57.8) * mm, "end": v(-26.25, 57) * mm});
            skLineSegment(sketch, "E61.MirrorCS", {"start": v(-31.25, 57) * mm, "end": v(-31.25, 57.8) * mm});
            skLineSegment(sketch, "E62.MirrorCS", {"start": v(-45.3, 57.8) * mm, "end": v(-45.3, 57) * mm});
            skLineSegment(sketch, "E63.MirrorCS", {"start": v(-50.3, 57) * mm, "end": v(-50.3, 57.8) * mm});
            skLineSegment(sketch, "E64", {"start": v(-20.6, 2.7) * mm, "end": v(-18, 2.7) * mm});
            skLineSegment(sketch, "E65", {"start": v(-18, 2.7) * mm, "end": v(-19.3, 2.7) * mm});
            skLineSegment(sketch, "E66", {"start": v(-19.3, 2.7) * mm, "end": v(-19.3, 0.8) * mm});
            skLineSegment(sketch, "E67", {"start": v(-19.3, 0.8) * mm, "end": v(-16.7, 0.8) * mm});
            skLineSegment(sketch, "E68", {"start": v(-16.7, 0.8) * mm, "end": v(-16.7, 1.6) * mm});
            skLineSegment(sketch, "E69", {"start": v(-16.7, 1.6) * mm, "end": v(-21.9, 1.6) * mm});
            skLineSegment(sketch, "E70", {"start": v(-21.9, 1.6) * mm, "end": v(-21.9, 0.8) * mm});
            skLineSegment(sketch, "E71", {"start": v(-21.9, 0.8) * mm, "end": v(-19.3, 0.8) * mm});
            skLineSegment(sketch, "E72", {"start": v(-39.8, 2.7) * mm, "end": v(-37.2, 2.7) * mm});
            skLineSegment(sketch, "E73", {"start": v(-37.2, 2.7) * mm, "end": v(-38.5, 2.7) * mm});
            skLineSegment(sketch, "E74", {"start": v(-38.5, 2.7) * mm, "end": v(-38.5, 0.8) * mm});
            skLineSegment(sketch, "E75", {"start": v(-38.5, 0.8) * mm, "end": v(-35.9, 0.8) * mm});
            skLineSegment(sketch, "E76", {"start": v(-35.9, 0.8) * mm, "end": v(-35.9, 1.6) * mm});
            skLineSegment(sketch, "E77", {"start": v(-35.9, 1.6) * mm, "end": v(-41.1, 1.6) * mm});
            skLineSegment(sketch, "E78", {"start": v(-41.1, 1.6) * mm, "end": v(-41.1, 0.8) * mm});
            skLineSegment(sketch, "E79", {"start": v(-41.1, 0.8) * mm, "end": v(-38.5, 0.8) * mm});
            skLineSegment(sketch, "E80.MirrorCS", {"start": v(-16.7, 56.2) * mm, "end": v(-21.9, 56.2) * mm});
            skLineSegment(sketch, "E81.MirrorCS", {"start": v(-21.9, 56.2) * mm, "end": v(-21.9, 57) * mm});
            skLineSegment(sketch, "E82.MirrorCS", {"start": v(-16.7, 57) * mm, "end": v(-16.7, 56.2) * mm});
            skLineSegment(sketch, "E83.MirrorCS", {"start": v(-35.9, 57) * mm, "end": v(-35.9, 56.2) * mm});
            skLineSegment(sketch, "E84.MirrorCS", {"start": v(-35.9, 56.2) * mm, "end": v(-41.1, 56.2) * mm});
            skLineSegment(sketch, "E85.MirrorCS", {"start": v(-41.1, 56.2) * mm, "end": v(-41.1, 57) * mm});
            skLineSegment(sketch, "E86.bottom", {"start": v(-0.8, 21.9) * mm, "end": v(-1.6, 21.9) * mm});
            skLineSegment(sketch, "E86.top", {"start": v(-0.8, 16.7) * mm, "end": v(-1.6, 16.7) * mm});
            skLineSegment(sketch, "E86.left", {"start": v(-0.8, 21.9) * mm, "end": v(-0.8, 16.7) * mm});
            skLineSegment(sketch, "E86.right", {"start": v(-1.6, 21.9) * mm, "end": v(-1.6, 16.7) * mm});
            skLineSegment(sketch, "E87.bottom", {"start": v(-1.6, 41.1) * mm, "end": v(-0.8, 41.1) * mm});
            skLineSegment(sketch, "E87.top", {"start": v(-1.6, 35.9) * mm, "end": v(-0.8, 35.9) * mm});
            skLineSegment(sketch, "E87.left", {"start": v(-1.6, 41.1) * mm, "end": v(-1.6, 35.9) * mm});
            skLineSegment(sketch, "E87.right", {"start": v(-0.8, 41.1) * mm, "end": v(-0.8, 35.9) * mm});
            skLineSegment(sketch, "E88.MirrorCS", {"start": v(-56.2, 41.1) * mm, "end": v(-56.2, 35.9) * mm});
            skLineSegment(sketch, "E89.MirrorCS", {"start": v(-56.2, 41.1) * mm, "end": v(-57, 41.1) * mm});
            skLineSegment(sketch, "E90.MirrorCS", {"start": v(-56.2, 35.9) * mm, "end": v(-57, 35.9) * mm});
            skLineSegment(sketch, "E91.MirrorCS", {"start": v(-57, 16.7) * mm, "end": v(-56.2, 16.7) * mm});
            skLineSegment(sketch, "E92.MirrorCS", {"start": v(-56.2, 21.9) * mm, "end": v(-56.2, 16.7) * mm});
            skLineSegment(sketch, "E93.MirrorCS", {"start": v(-57, 21.9) * mm, "end": v(-56.2, 21.9) * mm});
            skSolve(sketch);
        }
        {
            var Q0;
            {var subQ0=sQuery(id+"F2.wireOp",EDGE,"E58.MirrorCS");Q0=makeQuery(id+"F2.imprint","IMPRINT",FACE,{"disambiguationData":[TD([[makeQuery(id+"F2.imprint","IMPRINT",EDGE,{"derivedFrom":subQ0}),1.0]])]});}
            var Q1;
            {var subQ3=sQuery(id+"F2.wireOp",EDGE,"E61.MirrorCS");Q1=makeQuery(id+"F2.imprint","IMPRINT",FACE,{"disambiguationData":[TD([[makeQuery(id+"F2.imprint","IMPRINT",EDGE,{"derivedFrom":subQ3}),1.0]])]});}
            var Q2;
            {var subQ5=sQuery(id+"F2.wireOp",EDGE,"E54");Q2=makeQuery(id+"F2.imprint","IMPRINT",FACE,{"disambiguationData":[TD([[makeQuery(id+"F2.imprint","IMPRINT",EDGE,{"derivedFrom":subQ5}),-1.0]])]});}
            var Q3;
            {var subQ5=sQuery(id+"F2.wireOp",EDGE,"E57.1.0.0");Q3=makeQuery(id+"F2.imprint","IMPRINT",FACE,{"disambiguationData":[TD([[makeQuery(id+"F2.imprint","IMPRINT",EDGE,{"derivedFrom":subQ5}),-1.0]])]});}
            var Q4;
            {var subQ3=sQuery(id+"F2.wireOp",EDGE,"E43.MirrorCS");Q4=makeQuery(id+"F2.imprint","IMPRINT",FACE,{"disambiguationData":[TD([[makeQuery(id+"F2.imprint","IMPRINT",EDGE,{"derivedFrom":subQ3}),-1.0]])]});}
            var Q5;
            {var subQ3=sQuery(id+"F2.wireOp",EDGE,"E45.MirrorCS");Q5=makeQuery(id+"F2.imprint","IMPRINT",FACE,{"disambiguationData":[TD([[makeQuery(id+"F2.imprint","IMPRINT",EDGE,{"derivedFrom":subQ3}),-1.0]])]});}
            var Q6;
            {var subQ0=sQuery(id+"F2.wireOp",EDGE,"E41.0.1.0");Q6=makeQuery(id+"F2.imprint","IMPRINT",FACE,{"disambiguationData":[TD([[makeQuery(id+"F2.imprint","IMPRINT",EDGE,{"derivedFrom":subQ0}),1.0]])]});}
            var Q7;
            {var subQ4=sQuery(id+"F2.wireOp",EDGE,"E38.MirrorCS");Q7=makeQuery(id+"F2.imprint","IMPRINT",FACE,{"disambiguationData":[TD([[makeQuery(id+"F2.imprint","IMPRINT",EDGE,{"derivedFrom":subQ4}),1.0]])]});}
            var Q8;
            {var subQ4=sQuery(id+"F2.wireOp",EDGE,"E47.MirrorCS");Q8=makeQuery(id+"F2.imprint","IMPRINT",FACE,{"disambiguationData":[TD([[makeQuery(id+"F2.imprint","IMPRINT",EDGE,{"derivedFrom":subQ4}),-1.0]])]});}
            var Q9;
            {var subQ0=sQuery(id+"F2.wireOp",EDGE,"E41.0.2.0");Q9=makeQuery(id+"F2.imprint","IMPRINT",FACE,{"disambiguationData":[TD([[makeQuery(id+"F2.imprint","IMPRINT",EDGE,{"derivedFrom":subQ0}),1.0]])]});}
            var Q10;
            {var subQ4=sQuery(id+"F2.wireOp",EDGE,"E36");Q10=makeQuery(id+"F2.imprint","IMPRINT",FACE,{"disambiguationData":[TD([[makeQuery(id+"F2.imprint","IMPRINT",EDGE,{"derivedFrom":subQ4}),-1.0]])]});}
            var Q11;
            {var subQ0=sQuery(id+"F2.wireOp",EDGE,"E42.MirrorCS");Q11=makeQuery(id+"F2.imprint","IMPRINT",FACE,{"disambiguationData":[TD([[makeQuery(id+"F2.imprint","IMPRINT",EDGE,{"derivedFrom":subQ0}),1.0]])]});}
            var Q12;
            Q12=makeQuery(id+"F2.imprint","IMPRINT",FACE,{"disambiguationData":[TD([[makeQuery(id+"F2.imprint","IMPRINT",EDGE,{"derivedFrom":sQuery(id+"F2.wireOp",EDGE,"seCvFWz7-3Vyj-EDlB-MZ3c-75n9qILX0sIo.bottom")}),1.0]])]});
            var Q13;
            Q13=makeQuery(id+"F2.imprint","IMPRINT",FACE,{"disambiguationData":[TD([[makeQuery(id+"F2.imprint","IMPRINT",EDGE,{"derivedFrom":sQuery(id+"F2.wireOp",EDGE,"4fgsFxhj-Vw8K-A3UU-hoMM-U5Z05xPXw9eo.bottom")}),-1.0]])]});
            var Q14;
            Q14=makeQuery(id+"F2.imprint","IMPRINT",FACE,{"disambiguationData":[TD([[makeQuery(id+"F2.imprint","IMPRINT",EDGE,{"derivedFrom":sQuery(id+"F2.wireOp",EDGE,"8JcU31iA-pnQ1-UeEB-hfCA-LhXNwB3ENcUS.bottom")}),-1.0]])]});
            var Q15;
            Q15=makeQuery(id+"F2.imprint","IMPRINT",FACE,{"disambiguationData":[TD([[makeQuery(id+"F2.imprint","IMPRINT",EDGE,{"derivedFrom":sQuery(id+"F2.wireOp",EDGE,"OlrV4xQ8-PCdh-Lz6a-d3HF-mxwQSlMNRf3y.bottom")}),-1.0]])]});
            var Q16;
            Q16=makeQuery(id+"F2.imprint","IMPRINT",FACE,{"disambiguationData":[TD([[makeQuery(id+"F2.imprint","IMPRINT",EDGE,{"derivedFrom":sQuery(id+"F2.wireOp",EDGE,"ayyhUnhM-DQ2w-0yUz-URMn-H04yOfpyqTR6.bottom")}),-1.0]])]});
            var Q17;
            Q17=makeQuery(id+"F2.imprint","IMPRINT",FACE,{"disambiguationData":[TD([[makeQuery(id+"F2.imprint","IMPRINT",EDGE,{"derivedFrom":sQuery(id+"F2.wireOp",EDGE,"mYwaf8O3-GN9M-ZloA-LC7I-NsK6HDQISpYx.bottom")}),1.0]])]});
            var Q18;
            Q18=makeQuery(id+"F2.imprint","IMPRINT",FACE,{"disambiguationData":[TD([[makeQuery(id+"F2.imprint","IMPRINT",EDGE,{"derivedFrom":sQuery(id+"F2.wireOp",EDGE,"zB8xGJEq-JO7T-5BuP-HgzV-HP2KxO2sEsJY.bottom")}),-1.0]])]});
            var Q19;
            Q19=makeQuery(id+"F2.imprint","IMPRINT",FACE,{"disambiguationData":[TD([[makeQuery(id+"F2.imprint","IMPRINT",EDGE,{"derivedFrom":sQuery(id+"F2.wireOp",EDGE,"NLDKiq9c-kwNa-TPA2-ByV7-jquoLVFJqgiB.bottom")}),1.0]])]});
            var Q20;
            {var subQ0=sQuery(id+"F2.wireOp",EDGE,"E83.MirrorCS");Q20=makeQuery(id+"F2.imprint","IMPRINT",FACE,{"disambiguationData":[TD([[makeQuery(id+"F2.imprint","IMPRINT",EDGE,{"derivedFrom":subQ0}),-1.0]])]});}
            var Q21;
            Q21=makeQuery(id+"F2.imprint","IMPRINT",FACE,{"disambiguationData":[TD([[makeQuery(id+"F2.imprint","IMPRINT",EDGE,{"derivedFrom":sQuery(id+"F2.wireOp",EDGE,"E80.MirrorCS")}),-1.0]])]});
            var Q22;
            {var subQ4=sQuery(id+"F2.wireOp",EDGE,"hzmNtcyy-bsN6-4v00-7gln-cizqo3i05FAj.left");Q22=makeQuery(id+"F2.imprint","IMPRINT",FACE,{"disambiguationData":[TD([[makeQuery(id+"F2.imprint","IMPRINT",EDGE,{"derivedFrom":subQ4}),1.0]])]});}
            var Q23;
            {var subQ0=sQuery(id+"F2.wireOp",EDGE,"9bc7Yqau-rKPS-AFyk-DTsL-w0k6h2iHsBrv");Q23=makeQuery(id+"F2.imprint","IMPRINT",FACE,{"disambiguationData":[TD([[makeQuery(id+"F2.imprint","IMPRINT",EDGE,{"derivedFrom":subQ0}),1.0]])]});}
            var Q24;
            {var subQ0=sQuery(id+"F2.wireOp",EDGE,"uin3CZHS-8rT3-K8BR-KSBn-ANNy8O3vVnNV");Q24=makeQuery(id+"F2.imprint","IMPRINT",FACE,{"disambiguationData":[TD([[makeQuery(id+"F2.imprint","IMPRINT",EDGE,{"derivedFrom":subQ0}),-1.0]])]});}
            var Q25;
            {var subQ1=sQuery(id+"F2.wireOp",EDGE,"9bc7Yqau-rKPS-AFyk-DTsL-w0k6h2iHsBrv");Q25=makeQuery(id+"F2.imprint","IMPRINT",FACE,{"disambiguationData":[TD([[makeQuery(id+"F2.imprint","IMPRINT",EDGE,{"derivedFrom":subQ1}),-1.0]])]});}
            var Q26;
            {var subQ4=sQuery(id+"F2.wireOp",EDGE,"51b707c6-7d05-4d95-a325-fbbc0b48f4530.MirrorCS");Q26=makeQuery(id+"F2.imprint","IMPRINT",FACE,{"disambiguationData":[TD([[makeQuery(id+"F2.imprint","IMPRINT",EDGE,{"derivedFrom":subQ4}),-1.0]])]});}
            var Q27;
            {var subQ3=sQuery(id+"F2.wireOp",EDGE,"E78");Q27=makeQuery(id+"F2.imprint","IMPRINT",FACE,{"disambiguationData":[TD([[makeQuery(id+"F2.imprint","IMPRINT",EDGE,{"derivedFrom":subQ3}),1.0]])]});}
            var Q28;
            {var subQ3=sQuery(id+"F2.wireOp",EDGE,"E76");Q28=makeQuery(id+"F2.imprint","IMPRINT",FACE,{"disambiguationData":[TD([[makeQuery(id+"F2.imprint","IMPRINT",EDGE,{"derivedFrom":subQ3}),1.0]])]});}
            var Q29;
            {var subQ3=sQuery(id+"F2.wireOp",EDGE,"E70");Q29=makeQuery(id+"F2.imprint","IMPRINT",FACE,{"disambiguationData":[TD([[makeQuery(id+"F2.imprint","IMPRINT",EDGE,{"derivedFrom":subQ3}),1.0]])]});}
            var Q30;
            {var subQ3=sQuery(id+"F2.wireOp",EDGE,"E68");Q30=makeQuery(id+"F2.imprint","IMPRINT",FACE,{"disambiguationData":[TD([[makeQuery(id+"F2.imprint","IMPRINT",EDGE,{"derivedFrom":subQ3}),1.0]])]});}
            var Q31;
            {var subQ4=sQuery(id+"F2.wireOp",EDGE,"c7c54e78-877c-4306-874e-dcac1cb5a3220.MirrorCS");Q31=makeQuery(id+"F2.imprint","IMPRINT",FACE,{"disambiguationData":[TD([[makeQuery(id+"F2.imprint","IMPRINT",EDGE,{"derivedFrom":subQ4}),1.0]])]});}
            var Q32;
            {var subQ4=sQuery(id+"F2.wireOp",EDGE,"E88.MirrorCS");Q32=makeQuery(id+"F2.imprint","IMPRINT",FACE,{"disambiguationData":[TD([[makeQuery(id+"F2.imprint","IMPRINT",EDGE,{"derivedFrom":subQ4}),-1.0]])]});}
            var Q33;
            {var subQ0=sQuery(id+"F2.wireOp",EDGE,"E92.MirrorCS");Q33=makeQuery(id+"F2.imprint","IMPRINT",FACE,{"disambiguationData":[TD([[makeQuery(id+"F2.imprint","IMPRINT",EDGE,{"derivedFrom":subQ0}),-1.0]])]});}
            var Q34;
            {var subQ4=sQuery(id+"F2.wireOp",EDGE,"E87.left");Q34=makeQuery(id+"F2.imprint","IMPRINT",FACE,{"disambiguationData":[TD([[makeQuery(id+"F2.imprint","IMPRINT",EDGE,{"derivedFrom":subQ4}),1.0]])]});}
            var Q35;
            {var subQ4=sQuery(id+"F2.wireOp",EDGE,"E86.right");Q35=makeQuery(id+"F2.imprint","IMPRINT",FACE,{"disambiguationData":[TD([[makeQuery(id+"F2.imprint","IMPRINT",EDGE,{"derivedFrom":subQ4}),1.0]])]});}
            extrude(context, id + "F3", {"entities" : qUnion([Q0, Q1, Q2, Q3, Q4, Q5, Q6, Q7, Q8, Q9, Q10, Q11, Q12, Q13, Q14, Q15, Q16, Q17, Q18, Q19, Q20, Q21, Q22, Q23, Q24, Q25, Q26, Q27, Q28, Q29, Q30, Q31, Q32, Q33, Q34, Q35]), "operationType" : NewBodyOperationType.ADD, "depth" : 8.4 * mm, "offsetDistance" : 25 * mm});
        }
        {
            var Q0;
            {var subQ0=sQuery(id+"F2.wireOp",EDGE,"E46.MirrorCS");Q0=makeQuery(id+"F2.imprint","IMPRINT",FACE,{"disambiguationData":[TD([[makeQuery(id+"F2.imprint","IMPRINT",EDGE,{"derivedFrom":subQ0}),-1.0]])]});}
            var Q1;
            {var subQ0=sQuery(id+"F2.wireOp",EDGE,"E44.MirrorCS");Q1=makeQuery(id+"F2.imprint","IMPRINT",FACE,{"disambiguationData":[TD([[makeQuery(id+"F2.imprint","IMPRINT",EDGE,{"derivedFrom":subQ0}),-1.0]])]});}
            var Q2;
            {var subQ0=sQuery(id+"F2.wireOp",EDGE,"E42.MirrorCS");Q2=makeQuery(id+"F2.imprint","IMPRINT",FACE,{"disambiguationData":[TD([[makeQuery(id+"F2.imprint","IMPRINT",EDGE,{"derivedFrom":subQ0}),-1.0]])]});}
            var Q3;
            {var subQ0=sQuery(id+"F2.wireOp",EDGE,"E34");Q3=makeQuery(id+"F2.imprint","IMPRINT",FACE,{"disambiguationData":[TD([[makeQuery(id+"F2.imprint","IMPRINT",EDGE,{"derivedFrom":subQ0}),1.0]])]});}
            var Q4;
            {var subQ0=sQuery(id+"F2.wireOp",EDGE,"E34");Q4=makeQuery(id+"F2.imprint","IMPRINT",FACE,{"disambiguationData":[TD([[makeQuery(id+"F2.imprint","IMPRINT",EDGE,{"derivedFrom":subQ0}),-1.0]])]});}
            var Q5;
            {var subQ0=sQuery(id+"F2.wireOp",EDGE,"E41.0.1.0");Q5=makeQuery(id+"F2.imprint","IMPRINT",FACE,{"disambiguationData":[TD([[makeQuery(id+"F2.imprint","IMPRINT",EDGE,{"derivedFrom":subQ0}),-1.0]])]});}
            var Q6;
            {var subQ0=sQuery(id+"F2.wireOp",EDGE,"E41.0.2.0");Q6=makeQuery(id+"F2.imprint","IMPRINT",FACE,{"disambiguationData":[TD([[makeQuery(id+"F2.imprint","IMPRINT",EDGE,{"derivedFrom":subQ0}),-1.0]])]});}
            var Q7;
            {var subQ0=sQuery(id+"F2.wireOp",EDGE,"E62.MirrorCS");Q7=makeQuery(id+"F2.imprint","IMPRINT",FACE,{"disambiguationData":[TD([[makeQuery(id+"F2.imprint","IMPRINT",EDGE,{"derivedFrom":subQ0}),-1.0]])]});}
            var Q8;
            {var subQ0=sQuery(id+"F2.wireOp",EDGE,"E60.MirrorCS");Q8=makeQuery(id+"F2.imprint","IMPRINT",FACE,{"disambiguationData":[TD([[makeQuery(id+"F2.imprint","IMPRINT",EDGE,{"derivedFrom":subQ0}),-1.0]])]});}
            var Q9;
            {var subQ0=sQuery(id+"F2.wireOp",EDGE,"E58.MirrorCS");Q9=makeQuery(id+"F2.imprint","IMPRINT",FACE,{"disambiguationData":[TD([[makeQuery(id+"F2.imprint","IMPRINT",EDGE,{"derivedFrom":subQ0}),-1.0]])]});}
            var Q10;
            {var subQ0=sQuery(id+"F2.wireOp",EDGE,"E57.2.0.0");Q10=makeQuery(id+"F2.imprint","IMPRINT",FACE,{"disambiguationData":[TD([[makeQuery(id+"F2.imprint","IMPRINT",EDGE,{"derivedFrom":subQ0}),1.0]])]});}
            var Q11;
            {var subQ0=sQuery(id+"F2.wireOp",EDGE,"E40");Q11=makeQuery(id+"F2.imprint","IMPRINT",FACE,{"disambiguationData":[TD([[makeQuery(id+"F2.imprint","IMPRINT",EDGE,{"derivedFrom":subQ0}),1.0]])]});}
            var Q12;
            {var subQ0=sQuery(id+"F2.wireOp",EDGE,"E40");Q12=makeQuery(id+"F2.imprint","IMPRINT",FACE,{"disambiguationData":[TD([[makeQuery(id+"F2.imprint","IMPRINT",EDGE,{"derivedFrom":subQ0}),-1.0]])]});}
            var Q13;
            {var subQ0=sQuery(id+"F2.wireOp",EDGE,"E49");Q13=makeQuery(id+"F2.imprint","IMPRINT",FACE,{"disambiguationData":[TD([[makeQuery(id+"F2.imprint","IMPRINT",EDGE,{"derivedFrom":subQ0}),1.0]])]});}
            var Q14;
            {var subQ0=sQuery(id+"F2.wireOp",EDGE,"E49");Q14=makeQuery(id+"F2.imprint","IMPRINT",FACE,{"disambiguationData":[TD([[makeQuery(id+"F2.imprint","IMPRINT",EDGE,{"derivedFrom":subQ0}),-1.0]])]});}
            var Q15;
            {var subQ0=sQuery(id+"F2.wireOp",EDGE,"E41.0.1.1");Q15=makeQuery(id+"F2.imprint","IMPRINT",FACE,{"disambiguationData":[TD([[makeQuery(id+"F2.imprint","IMPRINT",EDGE,{"derivedFrom":subQ0}),1.0]])]});}
            extrude(context, id + "F4", {"entities" : qUnion([Q0, Q1, Q2, Q3, Q4, Q5, Q6, Q7, Q8, Q9, Q10, Q11, Q12, Q13, Q14, Q15]), "operationType" : NewBodyOperationType.ADD, "depth" : 4.4 * mm, "offsetDistance" : 25 * mm});
        }
        {
            var Q0;
            {var subQ0=sQuery(id+"F2.wireOp",EDGE,"E31.right");var subQ1=makeQuery(id+"F2.imprint","INTERSECT",VERTEX,{"derivedFrom":[subQ0,sQuery(id+"F2.wireOp",EDGE,"E46.MirrorCS")]});var subQ3=makeQuery(id+"F2.imprint","INTERSECT",VERTEX,{"derivedFrom":[subQ0,sQuery(id+"F2.wireOp",EDGE,"E44.MirrorCS")]});var subQ4=makeQuery(id+"F2.imprint","INTERSECT",VERTEX,{"derivedFrom":[subQ0,sQuery(id+"F2.wireOp",EDGE,"E45.MirrorCS")]});var subQ5=makeQuery(id+"F2.imprint","INTERSECT",VERTEX,{"derivedFrom":[subQ0,sQuery(id+"F2.wireOp",EDGE,"E42.MirrorCS")]});var subQ6=makeQuery(id+"F2.imprint","INTERSECT",VERTEX,{"derivedFrom":[subQ0,sQuery(id+"F2.wireOp",EDGE,"E43.MirrorCS")]});Q0=makeQuery(id+"F4.boolean.opBoolean","MERGE",FACE,{"derivedFrom":[makeQuery(id+"F3.boolean.opBoolean","MERGE",FACE,{"derivedFrom":[makeQuery(id+"F1.opExtrude","SWEPT_FACE",FACE,{"disambiguationData":[OSD([sQuery(id+"F0.wireOp",EDGE,"E12.right")])]}),makeQuery(id+"F3.opExtrude","SWEPT_FACE",FACE,{"disambiguationData":[OSD([subQ0]),TDD([makeQuery(id+"F2.imprint","IMPRINT",EDGE,{"disambiguationData":[TD([[makeQuery(id+"F2.imprint","INTERSECT",VERTEX,{"derivedFrom":[sQuery(id+"F2.wireOp",EDGE,"E31.bottom"),subQ0]}),-1.0]])],"derivedFrom":subQ0})])]}),makeQuery(id+"F3.opExtrude","SWEPT_FACE",FACE,{"disambiguationData":[OSD([subQ0]),TDD([makeQuery(id+"F2.imprint","IMPRINT",EDGE,{"disambiguationData":[TD([[subQ6,-1.0]])],"derivedFrom":subQ0})])]}),makeQuery(id+"F3.opExtrude","SWEPT_FACE",FACE,{"disambiguationData":[OSD([subQ0]),TDD([makeQuery(id+"F2.imprint","IMPRINT",EDGE,{"disambiguationData":[TD([[subQ4,-1.0]])],"derivedFrom":subQ0})])]}),makeQuery(id+"F3.opExtrude","SWEPT_FACE",FACE,{"disambiguationData":[OSD([subQ0]),TDD([makeQuery(id+"F2.imprint","IMPRINT",EDGE,{"disambiguationData":[TD([[makeQuery(id+"F2.imprint","INTERSECT",VERTEX,{"derivedFrom":[sQuery(id+"F2.wireOp",EDGE,"E31.top"),subQ0]}),1.0]])],"derivedFrom":subQ0})])]})]}),makeQuery(id+"F4.opExtrude","SWEPT_FACE",FACE,{"disambiguationData":[OSD([subQ0]),TDD([makeQuery(id+"F2.imprint","IMPRINT",EDGE,{"disambiguationData":[TD([[subQ5,-1.0]])],"derivedFrom":subQ0})])]}),makeQuery(id+"F4.opExtrude","SWEPT_FACE",FACE,{"disambiguationData":[OSD([subQ0]),TDD([makeQuery(id+"F2.imprint","IMPRINT",EDGE,{"disambiguationData":[TD([[subQ3,-1.0]])],"derivedFrom":subQ0})])]}),makeQuery(id+"F4.opExtrude","SWEPT_FACE",FACE,{"disambiguationData":[OSD([subQ0]),TDD([makeQuery(id+"F2.imprint","IMPRINT",EDGE,{"disambiguationData":[TD([[subQ1,-1.0]])],"derivedFrom":subQ0})])]})]});}
            var sketch = newSketch(context, id + "F5", { "sketchPlane" : qUnion([Q0])});
            skCircle(sketch, "E94", {"center": v(-19.23, 6) * mm, "radius": 1.25 * mm});
            skLineSegment(sketch, "E95", {"start": v(-26.25, 6) * mm, "end": v(-19.23, 6) * mm});
            skLineSegment(sketch, "E96", {"start": v(-19.23, 6) * mm, "end": v(-12.2, 6) * mm});
            skLineSegment(sketch, "E97", {"start": v(-28.75, 6) * mm, "end": v(-28.9, 0) * mm});
            skCircle(sketch, "E98.MirrorC", {"center": v(-38.26, 6.48) * mm, "radius": 1.25 * mm});
            skSolve(sketch);
        }
        {
            var Q0;
            Q0=makeQuery(id+"F5.imprint","IMPRINT",FACE,{"disambiguationData":[TD([[makeQuery(id+"F5.imprint","IMPRINT",EDGE,{"derivedFrom":sQuery(id+"F5.wireOp",EDGE,"E98.MirrorC")}),-1.0]])]});
            var Q1;
            {var subQ0=sQuery(id+"F5.wireOp",EDGE,"E95");var subQ1=sQuery(id+"F5.wireOp",EDGE,"E94");var subQ2=makeQuery(id+"F5.imprint","INTERSECT",VERTEX,{"derivedFrom":[subQ1,subQ0]});Q1=makeQuery(id+"F5.imprint","IMPRINT",FACE,{"disambiguationData":[TD([[makeQuery(id+"F5.imprint","IMPRINT",EDGE,{"disambiguationData":[TD([[subQ2,1.0]])],"derivedFrom":subQ1}),1.0]])]});}
            var Q2;
            {var subQ0=sQuery(id+"F5.wireOp",EDGE,"E95");var subQ1=sQuery(id+"F5.wireOp",EDGE,"E94");var subQ2=makeQuery(id+"F5.imprint","INTERSECT",VERTEX,{"derivedFrom":[subQ1,subQ0]});Q2=makeQuery(id+"F5.imprint","IMPRINT",FACE,{"disambiguationData":[TD([[makeQuery(id+"F5.imprint","IMPRINT",EDGE,{"disambiguationData":[TD([[subQ2,-1.0]])],"derivedFrom":subQ1}),1.0]])]});}
            extrude(context, id + "F6", {"entities" : qUnion([Q0, Q1, Q2]), "operationType" : NewBodyOperationType.REMOVE, "endBound" : BoundingType.THROUGH_ALL, "oppositeDirection" : true, "depth" : 25 * mm, "offsetDistance" : 25 * mm});
        }
        {
            var Q0;
            {var subQ0=sQuery(id+"F2.wireOp",EDGE,"E31.bottom");var subQ1=makeQuery(id+"F2.imprint","INTERSECT",VERTEX,{"derivedFrom":[subQ0,sQuery(id+"F2.wireOp",EDGE,"E57.2.0.0")]});var subQ3=makeQuery(id+"F2.imprint","INTERSECT",VERTEX,{"derivedFrom":[subQ0,sQuery(id+"F2.wireOp",EDGE,"E40")]});var subQ4=makeQuery(id+"F2.imprint","INTERSECT",VERTEX,{"derivedFrom":[subQ0,sQuery(id+"F2.wireOp",EDGE,"E57.1.0.0")]});var subQ6=makeQuery(id+"F2.imprint","INTERSECT",VERTEX,{"derivedFrom":[subQ0,sQuery(id+"F2.wireOp",EDGE,"E49")]});var subQ7=makeQuery(id+"F2.imprint","INTERSECT",VERTEX,{"derivedFrom":[subQ0,sQuery(id+"F2.wireOp",EDGE,"E54")]});Q0=makeQuery(id+"F4.boolean.opBoolean","MERGE",FACE,{"derivedFrom":[makeQuery(id+"F3.boolean.opBoolean","MERGE",FACE,{"derivedFrom":[makeQuery(id+"F1.opExtrude","SWEPT_FACE",FACE,{"disambiguationData":[OSD([sQuery(id+"F0.wireOp",EDGE,"E12.bottom")])]}),makeQuery(id+"F3.opExtrude","SWEPT_FACE",FACE,{"disambiguationData":[OSD([subQ0]),TDD([makeQuery(id+"F2.imprint","IMPRINT",EDGE,{"disambiguationData":[TD([[makeQuery(id+"F2.imprint","INTERSECT",VERTEX,{"derivedFrom":[subQ0,sQuery(id+"F2.wireOp",EDGE,"E31.left")]}),-1.0]])],"derivedFrom":subQ0})])]}),makeQuery(id+"F3.opExtrude","SWEPT_FACE",FACE,{"disambiguationData":[OSD([subQ0]),TDD([makeQuery(id+"F2.imprint","IMPRINT",EDGE,{"disambiguationData":[TD([[subQ7,-1.0]])],"derivedFrom":subQ0})])]}),makeQuery(id+"F3.opExtrude","SWEPT_FACE",FACE,{"disambiguationData":[OSD([subQ0]),TDD([makeQuery(id+"F2.imprint","IMPRINT",EDGE,{"disambiguationData":[TD([[subQ4,-1.0]])],"derivedFrom":subQ0})])]}),makeQuery(id+"F3.opExtrude","SWEPT_FACE",FACE,{"disambiguationData":[OSD([subQ0]),TDD([makeQuery(id+"F2.imprint","IMPRINT",EDGE,{"disambiguationData":[TD([[makeQuery(id+"F2.imprint","INTERSECT",VERTEX,{"derivedFrom":[subQ0,sQuery(id+"F2.wireOp",EDGE,"E31.right")]}),1.0]])],"derivedFrom":subQ0})])]})]}),makeQuery(id+"F4.opExtrude","SWEPT_FACE",FACE,{"disambiguationData":[OSD([subQ0]),TDD([makeQuery(id+"F2.imprint","IMPRINT",EDGE,{"disambiguationData":[TD([[subQ6,1.0]])],"derivedFrom":subQ0}),makeQuery(id+"F2.imprint","IMPRINT",EDGE,{"disambiguationData":[TD([[subQ6,-1.0]])],"derivedFrom":subQ0})])]}),makeQuery(id+"F4.opExtrude","SWEPT_FACE",FACE,{"disambiguationData":[OSD([subQ0]),TDD([makeQuery(id+"F2.imprint","IMPRINT",EDGE,{"disambiguationData":[TD([[subQ3,1.0]])],"derivedFrom":subQ0}),makeQuery(id+"F2.imprint","IMPRINT",EDGE,{"disambiguationData":[TD([[subQ3,-1.0]])],"derivedFrom":subQ0})])]}),makeQuery(id+"F4.opExtrude","SWEPT_FACE",FACE,{"disambiguationData":[OSD([subQ0]),TDD([makeQuery(id+"F2.imprint","IMPRINT",EDGE,{"disambiguationData":[TD([[subQ1,1.0]])],"derivedFrom":subQ0})])]})]});}
            var sketch = newSketch(context, id + "F7", { "sketchPlane" : qUnion([Q0])});
            skCircle(sketch, "E99", {"center": v(-19.23, 6) * mm, "radius": 1.25 * mm});
            skLineSegment(sketch, "E100", {"start": v(-19.23, 6) * mm, "end": v(-26.25, 6) * mm});
            skLineSegment(sketch, "E101", {"start": v(-19.23, 6) * mm, "end": v(-12.2, 6) * mm});
            skLineSegment(sketch, "E102", {"start": v(-28.75, 6) * mm, "end": v(-28.75, 0) * mm});
            skCircle(sketch, "E103.MirrorC", {"center": v(-38.28, 6) * mm, "radius": 1.25 * mm});
            skSolve(sketch);
        }
        {
            var Q0;
            {var subQ0=sQuery(id+"F7.wireOp",EDGE,"E100");var subQ1=sQuery(id+"F7.wireOp",EDGE,"E99");var subQ2=makeQuery(id+"F7.imprint","INTERSECT",VERTEX,{"derivedFrom":[subQ1,subQ0]});Q0=makeQuery(id+"F7.imprint","IMPRINT",FACE,{"disambiguationData":[TD([[makeQuery(id+"F7.imprint","IMPRINT",EDGE,{"disambiguationData":[TD([[subQ2,1.0]])],"derivedFrom":subQ1}),1.0]])]});}
            var Q1;
            {var subQ0=sQuery(id+"F7.wireOp",EDGE,"E100");var subQ1=sQuery(id+"F7.wireOp",EDGE,"E99");var subQ2=makeQuery(id+"F7.imprint","INTERSECT",VERTEX,{"derivedFrom":[subQ1,subQ0]});Q1=makeQuery(id+"F7.imprint","IMPRINT",FACE,{"disambiguationData":[TD([[makeQuery(id+"F7.imprint","IMPRINT",EDGE,{"disambiguationData":[TD([[subQ2,-1.0]])],"derivedFrom":subQ1}),1.0]])]});}
            var Q2;
            Q2=makeQuery(id+"F7.imprint","IMPRINT",FACE,{"disambiguationData":[TD([[makeQuery(id+"F7.imprint","IMPRINT",EDGE,{"derivedFrom":sQuery(id+"F7.wireOp",EDGE,"bce639fc-65aa-4438-8615-208144ccd1130.MirrorC")}),-1.0]])]});
            var Q3;
            Q3=makeQuery(id+"F7.imprint","IMPRINT",FACE,{"disambiguationData":[TD([[makeQuery(id+"F7.imprint","IMPRINT",EDGE,{"derivedFrom":sQuery(id+"F7.wireOp",EDGE,"E103.MirrorC")}),-1.0]])]});
            extrude(context, id + "F8", {"entities" : qUnion([Q0, Q1, Q2, Q3]), "operationType" : NewBodyOperationType.REMOVE, "endBound" : BoundingType.THROUGH_ALL, "oppositeDirection" : true, "depth" : 25 * mm, "offsetDistance" : 25 * mm});
        }
    });
